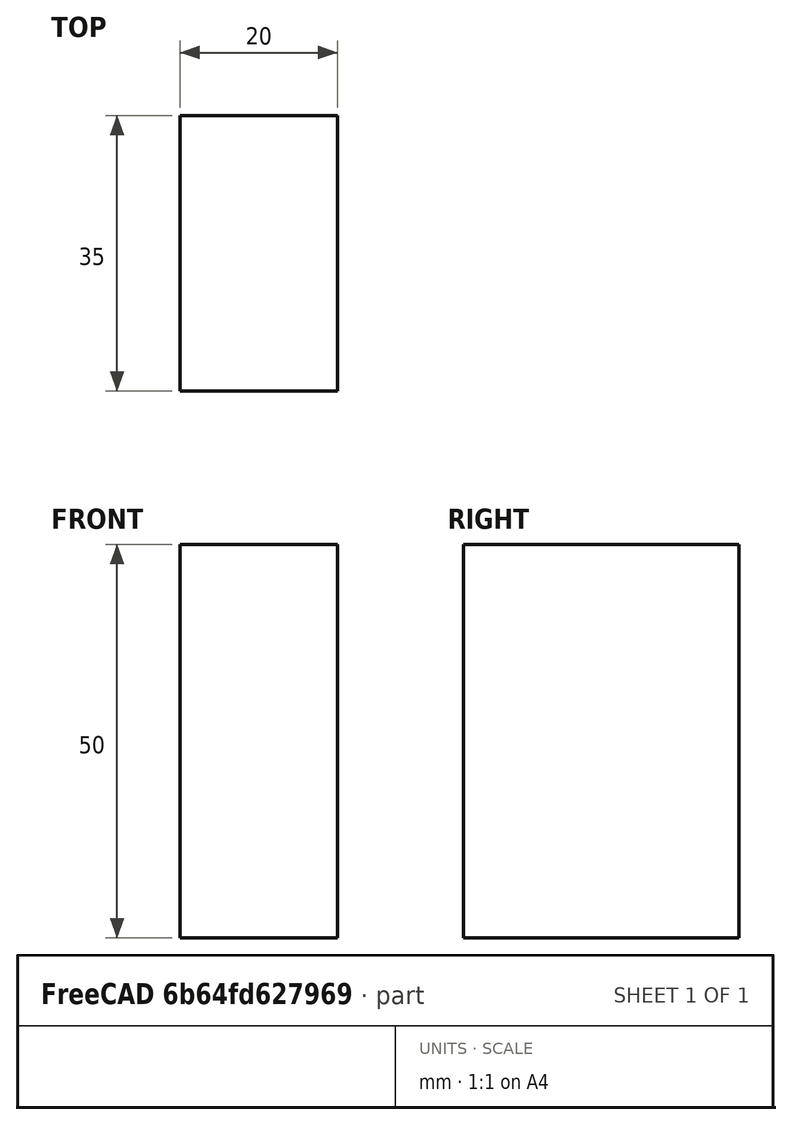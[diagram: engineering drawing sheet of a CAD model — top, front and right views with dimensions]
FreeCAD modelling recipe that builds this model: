
FCSTD DOCUMENT  (FreeCAD 0.19R24276 (Git))
Label: din-rail-mounting-bracket
License: All rights reserved
LicenseURL: http://en.wikipedia.org/wiki/All_rights_reserved
objects: Sketcher::SketchObject×1, PartDesign::Pad×1, PartDesign::Body×1
note: 4 computed .brp shape members not serialized (recipe doc carries the construction recipe); baked Part::Feature solids carry a one-line shape summary decoded from their .brp

FEATURE [Sketcher::SketchObject] Sketch
  FullyConstrained = true
  MapMode = 5
  Support = -> [XY_Plane]
  sketch-geometry (4):
    g0: LineSegment StartX=-10 StartY=17.5 StartZ=0 EndX=10 EndY=17.5 EndZ=0
    g1: LineSegment StartX=10 StartY=17.5 StartZ=0 EndX=10 EndY=-17.5 EndZ=0
    g2: LineSegment StartX=10 StartY=-17.5 StartZ=0 EndX=-10 EndY=-17.5 EndZ=0
    g3: LineSegment StartX=-10 StartY=-17.5 StartZ=0 EndX=-10 EndY=17.5 EndZ=0
  constraints (12):
    c: Coincident(g0,g1)
    c: Coincident(g1,g2)
    c: Coincident(g2,g3)
    c: Coincident(g3,g0)
    c: Horizontal(g0)
    c: Horizontal(g2)
    c: Vertical(g1)
    c: Vertical(g3)
    c: DistanceY(g-1,g0) = 17.5
    c: DistanceY(g2,g-1) = 17.5
    c: DistanceX(g0,g-1) = 10
    c: DistanceX(g-1,g1) = 10
FEATURE [PartDesign::Pad] Pad
  Direction = (1,1,1)
  Length = 50
  Length2 = 100
  Profile = -> Sketch
  Type = 0
FEATURE [PartDesign::Body] Body
  Group = -> [Sketch,Pad]
  Origin = -> Origin
  Tip = -> Pad
